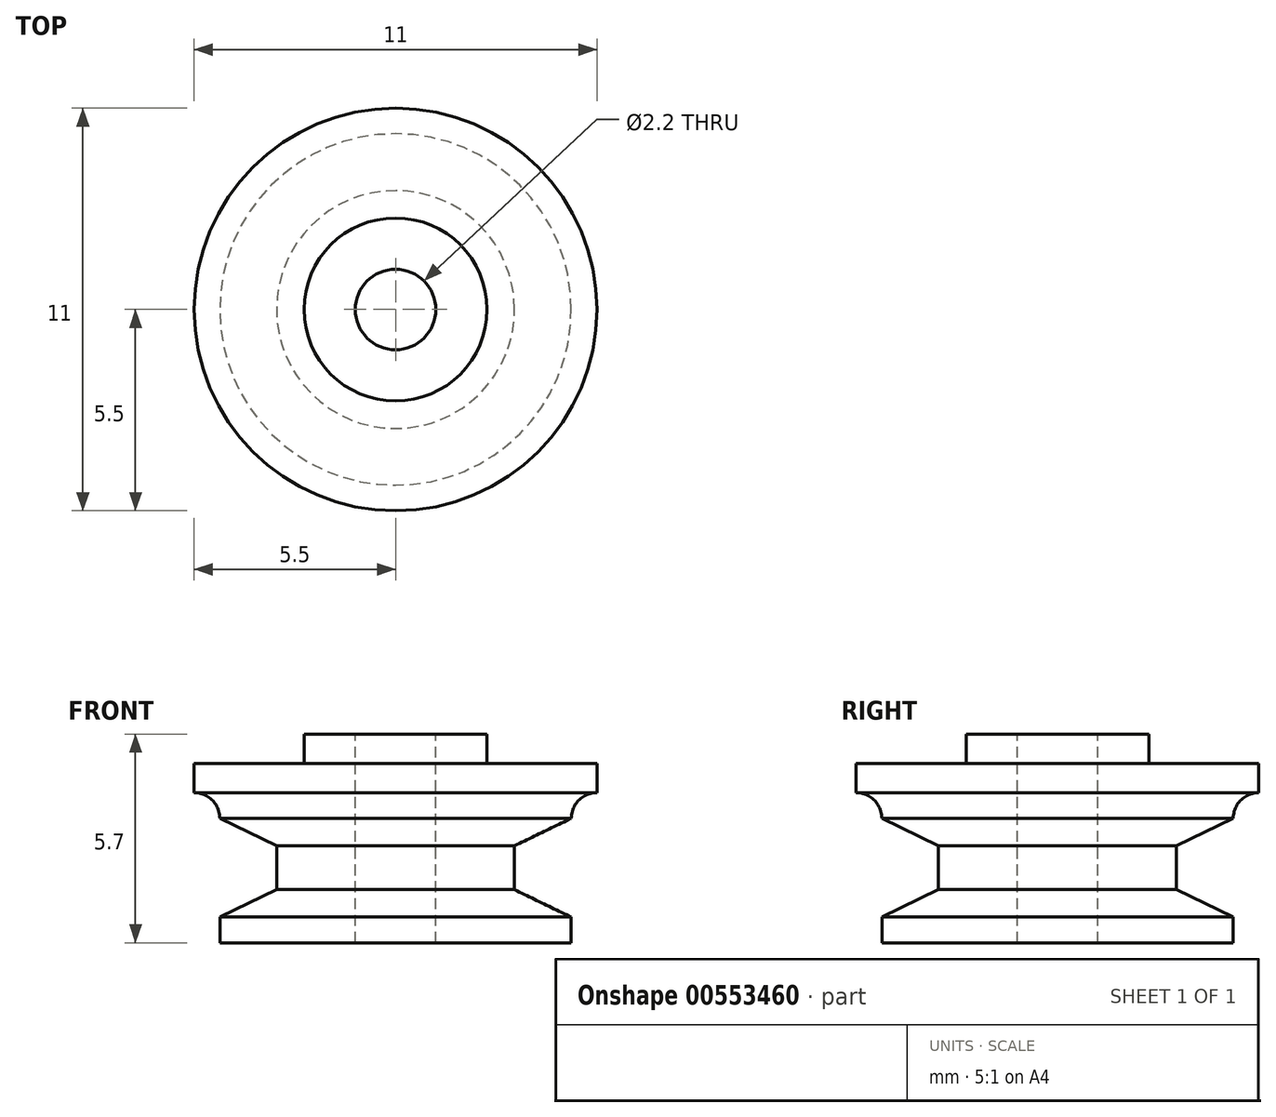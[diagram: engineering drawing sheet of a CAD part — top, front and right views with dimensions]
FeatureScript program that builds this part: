
annotation { "Feature Type Name" : "Feature", "Feature Type Description" : "" }
export const myFeature = defineFeature(function(context is Context, id is Id, definition is map)
    precondition{}
    {
        {
            var Q0;
            Q0=qCreatedBy(makeId("Front.planeOp"),FACE);
            var sketch = newSketch(context, id + "F0", { "sketchPlane" : qUnion([Q0])});
            skLineSegment(sketch, "E0", {"start": v(0, 0) * mm, "end": v(-4.8, 0) * mm});
            skLineSegment(sketch, "E1", {"start": v(-4.8, 0) * mm, "end": v(-4.8, 0.7) * mm});
            skLineSegment(sketch, "E2", {"start": v(-4.8, 0.7) * mm, "end": v(-3.25, 1.45) * mm});
            skLineSegment(sketch, "E3", {"start": v(-3.25, 1.45) * mm, "end": v(-3.25, 2.65) * mm});
            skLineSegment(sketch, "E4", {"start": v(-3.25, 2.65) * mm, "end": v(-4.8, 3.4) * mm});
            skLineSegment(sketch, "E5", {"start": v(-4.8, 3.4) * mm, "end": v(-4.8, 4.1) * mm});
            skLineSegment(sketch, "E6", {"start": v(-4.8, 4.1) * mm, "end": v(-5.5, 4.1) * mm});
            skLineSegment(sketch, "E7", {"start": v(-5.5, 4.1) * mm, "end": v(-5.5, 4.9) * mm});
            skLineSegment(sketch, "E8", {"start": v(-5.5, 4.9) * mm, "end": v(-2.5, 4.9) * mm});
            skLineSegment(sketch, "E9", {"start": v(-2.5, 4.9) * mm, "end": v(-2.5, 5.7) * mm});
            skLineSegment(sketch, "E10", {"start": v(-2.5, 5.7) * mm, "end": v(0, 5.7) * mm});
            skLineSegment(sketch, "E11", {"start": v(0, 5.7) * mm, "end": v(0, 0) * mm});
            skLineSegment(sketch, "E12", {"start": v(-9.92, 2.05) * mm, "end": v(5.15, 2.05) * mm, "construction": true});
            skSolve(sketch);
        }
        {
            var Q0;
            Q0 = qSketchRegion(id + "F0", true);
            var Q1;
            Q1=sQuery(id+"F0.wireOp",EDGE,"E11");
            revolve(context, id + "F1", {"entities" : qUnion([Q0]), "axis" : qUnion([Q1]), "revolveType" : RevolveType.FULL});
        }
        {
            var Q0;
            Q0=makeQuery(id+"F1.opRevolve","SWEPT_EDGE",EDGE,{"disambiguationData":[OSD([sQuery(id+"F0.wireOp",EDGE,"E5"),sQuery(id+"F0.wireOp",EDGE,"E6")])]});
            fillet(context, id + "F2", {"entities" : qUnion([Q0]), "radius" : 0.7 * mm, "tangentPropagation" : true, "allowEdgeOverflow" : false});
        }
        {
            var Q0;
            Q0=makeQuery(id+"F1.opRevolve","SWEPT_FACE",FACE,{"disambiguationData":[OSD([sQuery(id+"F0.wireOp",EDGE,"E10")])]});
            var sketch = newSketch(context, id + "F3", { "sketchPlane" : qUnion([Q0])});
            skCircle(sketch, "E13", {"center": v(0, 0) * mm, "radius": 1.1 * mm});
            skSolve(sketch);
        }
        {
            var Q0;
            Q0 = qSketchRegion(id + "F3", true);
            extrude(context, id + "F4", {"entities" : qUnion([Q0]), "operationType" : NewBodyOperationType.REMOVE, "endBound" : BoundingType.THROUGH_ALL, "oppositeDirection" : true, "depth" : 0.8 * mm, "offsetDistance" : 25 * mm});
        }
    });
